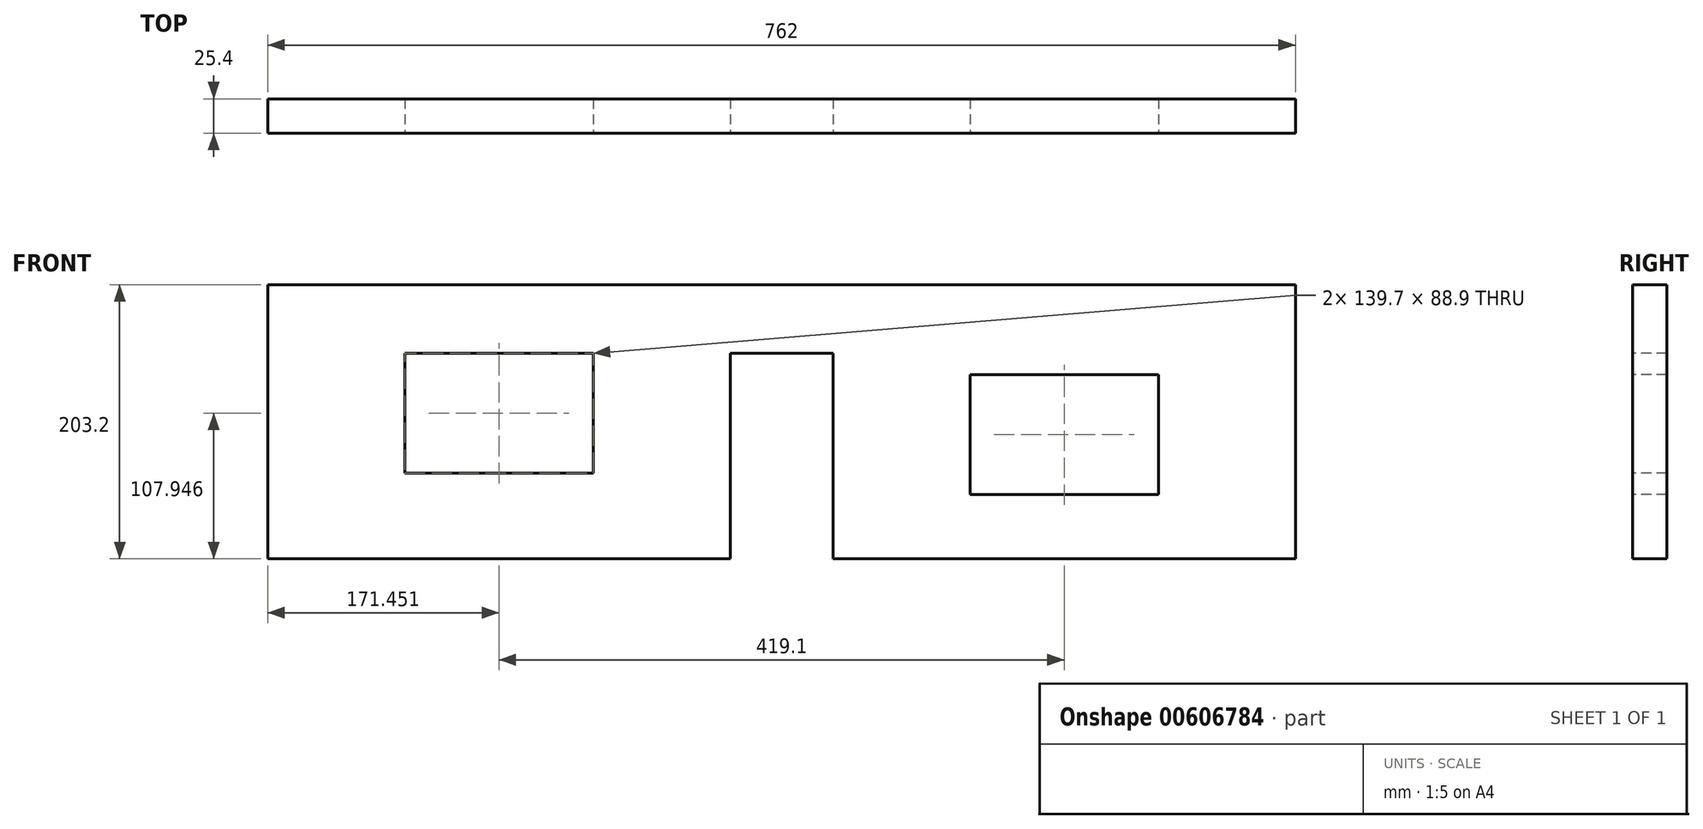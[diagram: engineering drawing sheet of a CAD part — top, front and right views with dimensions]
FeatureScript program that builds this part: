
annotation { "Feature Type Name" : "Feature", "Feature Type Description" : "" }
export const myFeature = defineFeature(function(context is Context, id is Id, definition is map)
    precondition{}
    {
        {
            var Q0;
            Q0=qCreatedBy(makeId("Front.planeOp"),FACE);
            var sketch = newSketch(context, id + "F0", { "sketchPlane" : qUnion([Q0])});
            skLineSegment(sketch, "E0.bottom", {"start": v(-382.35, -187.81) * mm, "end": v(379.65, -187.81) * mm});
            skLineSegment(sketch, "E0.top", {"start": v(-382.35, 15.39) * mm, "end": v(379.65, 15.39) * mm});
            skLineSegment(sketch, "E0.left", {"start": v(-382.35, -187.81) * mm, "end": v(-382.35, 15.39) * mm});
            skLineSegment(sketch, "E0.right", {"start": v(379.65, -187.81) * mm, "end": v(379.65, 15.39) * mm});
            skSolve(sketch);
        }
        {
            var Q0;
            Q0 = qSketchRegion(id + "F0", true);
            extrude(context, id + "F1", {"entities" : qUnion([Q0]), "depth" : 25.4 * mm, "offsetDistance" : 25.4 * mm});
        }
        {
            var Q0;
            Q0=makeQuery(id+"F1.opExtrude","CAP_FACE",FACE,{"disambiguationData":[OSD([sQuery(id+"F0.wireOp",EDGE,"E0.bottom"),sQuery(id+"F0.wireOp",EDGE,"E0.top"),sQuery(id+"F0.wireOp",EDGE,"E0.left"),sQuery(id+"F0.wireOp",EDGE,"E0.right")])],"isStart":false});
            var sketch = newSketch(context, id + "F2", { "sketchPlane" : qUnion([Q0])});
            skLineSegment(sketch, "E1.bottom", {"start": v(-39.45, -187.81) * mm, "end": v(36.75, -187.81) * mm});
            skLineSegment(sketch, "E1.top", {"start": v(-39.45, -35.41) * mm, "end": v(36.75, -35.41) * mm});
            skLineSegment(sketch, "E1.left", {"start": v(-39.45, -187.81) * mm, "end": v(-39.45, -35.41) * mm});
            skLineSegment(sketch, "E1.right", {"start": v(36.75, -187.81) * mm, "end": v(36.75, -35.41) * mm});
            skLineSegment(sketch, "E2.bottom", {"start": v(-280.75, -124.31) * mm, "end": v(-141.05, -124.31) * mm});
            skLineSegment(sketch, "E2.top", {"start": v(-280.75, -35.41) * mm, "end": v(-141.05, -35.41) * mm});
            skLineSegment(sketch, "E2.left", {"start": v(-280.75, -124.31) * mm, "end": v(-280.75, -35.41) * mm});
            skLineSegment(sketch, "E2.right", {"start": v(-141.05, -124.31) * mm, "end": v(-141.05, -35.41) * mm});
            skLineSegment(sketch, "E3.bottom", {"start": v(138.35, -51.44) * mm, "end": v(278.05, -51.44) * mm});
            skLineSegment(sketch, "E3.top", {"start": v(138.35, -140.34) * mm, "end": v(278.05, -140.34) * mm});
            skLineSegment(sketch, "E3.left", {"start": v(138.35, -51.44) * mm, "end": v(138.35, -140.34) * mm});
            skLineSegment(sketch, "E3.right", {"start": v(278.05, -51.44) * mm, "end": v(278.05, -140.34) * mm});
            skSolve(sketch);
        }
        {
            var Q0;
            Q0=makeQuery(id+"F2.imprint","IMPRINT",FACE,{"disambiguationData":[TD([[makeQuery(id+"F2.imprint","IMPRINT",EDGE,{"derivedFrom":sQuery(id+"F2.wireOp",EDGE,"E2.bottom")}),1.0]])]});
            extrude(context, id + "F3", {"entities" : qUnion([Q0]), "operationType" : NewBodyOperationType.REMOVE, "oppositeDirection" : true, "depth" : 50.8 * mm, "offsetDistance" : 25.4 * mm});
        }
        {
            var Q0;
            Q0=makeQuery(id+"F2.imprint","IMPRINT",FACE,{"disambiguationData":[TD([[makeQuery(id+"F2.imprint","IMPRINT",EDGE,{"derivedFrom":sQuery(id+"F2.wireOp",EDGE,"E1.bottom")}),1.0]])]});
            extrude(context, id + "F4", {"entities" : qUnion([Q0]), "operationType" : NewBodyOperationType.REMOVE, "oppositeDirection" : true, "depth" : 50.8 * mm, "offsetDistance" : 25.4 * mm});
        }
        {
            var Q0;
            Q0=makeQuery(id+"F2.imprint","IMPRINT",FACE,{"disambiguationData":[TD([[makeQuery(id+"F2.imprint","IMPRINT",EDGE,{"derivedFrom":sQuery(id+"F2.wireOp",EDGE,"E3.bottom")}),-1.0]])]});
            extrude(context, id + "F5", {"entities" : qUnion([Q0]), "operationType" : NewBodyOperationType.REMOVE, "oppositeDirection" : true, "depth" : 50.8 * mm, "offsetDistance" : 25.4 * mm});
        }
    });
